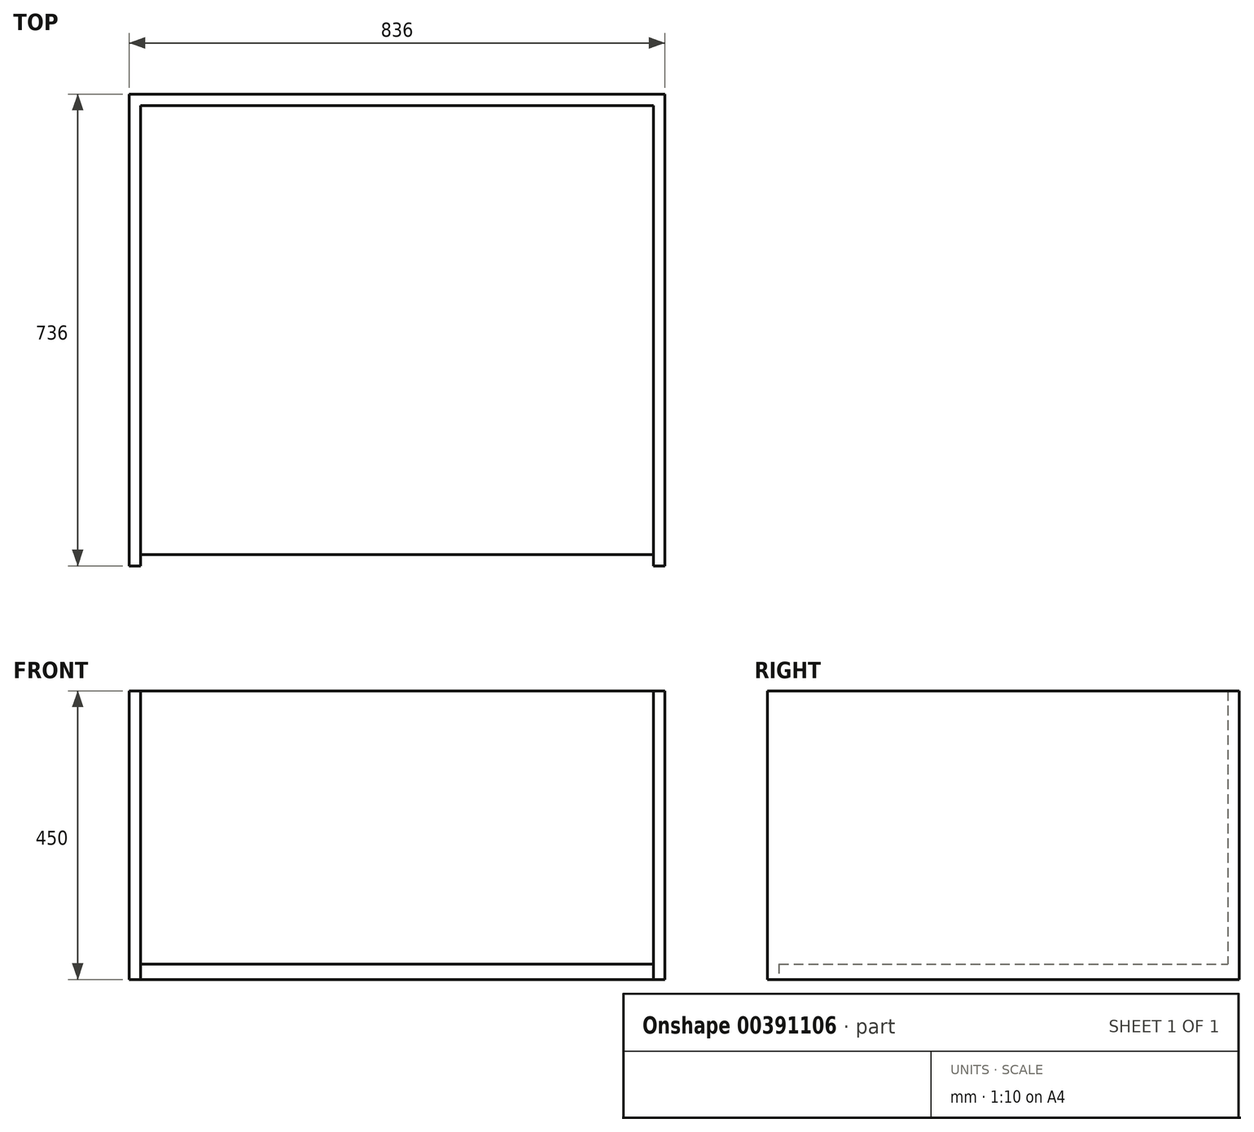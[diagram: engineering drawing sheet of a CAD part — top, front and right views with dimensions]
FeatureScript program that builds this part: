
annotation { "Feature Type Name" : "Feature", "Feature Type Description" : "" }
export const myFeature = defineFeature(function(context is Context, id is Id, definition is map)
    precondition{}
    {
        {
            var Q0;
            Q0=qCreatedBy(makeId("Top.planeOp"),FACE);
            var sketch = newSketch(context, id + "F0", { "sketchPlane" : qUnion([Q0])});
            skLineSegment(sketch, "E0.bottom", {"start": v(400, -350) * mm, "end": v(-400, -350) * mm});
            skLineSegment(sketch, "E0.top", {"start": v(400, 350) * mm, "end": v(-400, 350) * mm});
            skLineSegment(sketch, "E0.left", {"start": v(400, -350) * mm, "end": v(400, 350) * mm});
            skLineSegment(sketch, "E0.right", {"start": v(-400, -350) * mm, "end": v(-400, 350) * mm});
            skPoint(sketch, "E0.middle", {"position": v(0, 0) * mm});
            skPoint(sketch, "E1", {"position": v(-400, 0) * mm});
            skSolve(sketch);
        }
        {
            var Q0;
            {var subQ0=sQuery(id+"F0.wireOp",EDGE,"E0.bottom");Q0=makeQuery(id+"F0.imprint","IMPRINT",FACE,{"disambiguationData":[TD([[makeQuery(id+"F0.imprint","IMPRINT",EDGE,{"derivedFrom":subQ0}),-1.0]])]});}
            extrude(context, id + "F1", {"entities" : qUnion([Q0]), "depth" : 24 * mm});
        }
        {
            var Q0;
            Q0=qCreatedBy(makeId("Top.planeOp"),FACE);
            var sketch = newSketch(context, id + "F2", { "sketchPlane" : qUnion([Q0])});
            skLineSegment(sketch, "E2.bottom", {"start": v(400, 368) * mm, "end": v(418, 368) * mm});
            skLineSegment(sketch, "E2.top", {"start": v(400, -368) * mm, "end": v(418, -368) * mm});
            skLineSegment(sketch, "E2.left", {"start": v(400, 368) * mm, "end": v(400, -368) * mm});
            skLineSegment(sketch, "E2.right", {"start": v(418, 368) * mm, "end": v(418, -368) * mm});
            skPoint(sketch, "E3", {"position": v(400, 0) * mm});
            skSolve(sketch);
        }
        {
            var Q0;
            Q0 = qSketchRegion(id + "F2", true);
            extrude(context, id + "F3", {"entities" : qUnion([Q0]), "operationType" : NewBodyOperationType.ADD, "depth" : 450 * mm});
        }
        {
            var Q0;
            Q0=qCreatedBy(makeId("Top.planeOp"),FACE);
            var sketch = newSketch(context, id + "F4", { "sketchPlane" : qUnion([Q0])});
            skLineSegment(sketch, "E4.bottom", {"start": v(-400, 368) * mm, "end": v(400, 368) * mm});
            skLineSegment(sketch, "E4.top", {"start": v(-400, 350) * mm, "end": v(400, 350) * mm});
            skLineSegment(sketch, "E4.left", {"start": v(-400, 368) * mm, "end": v(-400, 350) * mm});
            skLineSegment(sketch, "E4.right", {"start": v(400, 368) * mm, "end": v(400, 350) * mm});
            skPoint(sketch, "E5", {"position": v(0, 350) * mm});
            skSolve(sketch);
        }
        {
            var Q0;
            Q0=makeQuery(id+"F1.opExtrude","SWEPT_BODY",BODY,{"disambiguationData":[OSD([sQuery(id+"F0.wireOp",EDGE,"E0.bottom"),sQuery(id+"F0.wireOp",EDGE,"E0.top"),sQuery(id+"F0.wireOp",EDGE,"E0.left"),sQuery(id+"F0.wireOp",EDGE,"E0.right")])]});
            var Q1;
            Q1=qCreatedBy(makeId("Right.planeOp"),FACE);
            mirror(context, id + "F5", {"operationType" : NewBodyOperationType.ADD, "entities" : qUnion([Q0]), "mirrorPlane" : qUnion([Q1])});
        }
        {
            var Q0;
            Q0 = qSketchRegion(id + "F4", true);
            extrude(context, id + "F6", {"entities" : qUnion([Q0]), "operationType" : NewBodyOperationType.ADD, "depth" : 450 * mm});
        }
    });
